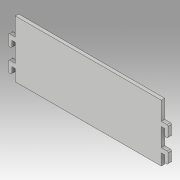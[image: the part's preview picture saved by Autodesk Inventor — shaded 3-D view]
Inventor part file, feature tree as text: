
AUTODESK INVENTOR PART (.ipt)
format: ipt  version: 2019.3 (Build 233278000, 278)  size: 138,240 bytes
history: native  units: mm
features: extrude x1, sketch x1
ambient origin geometry x8: Origin, YZ Plane, XZ Plane, XY Plane, X Axis, Y Axis, Z Axis, Center Point
bodies: Solid1 (feature_tree)
feature tree (2):
  extrude  "Extrusion1"  Depth=4.0mm
  sketch  "Sketch1"  dims[d0=10.0mm d1=4.0mm d2=3.0mm d3=3.0mm d6=10.0mm d7=4.0mm d8=30.0mm d9=50.0mm d11=1.0mm d12=64.0mm d13=64.0mm d14=6.0mm d15=6.0mm d16=3.0mm d17=0.0mm]
